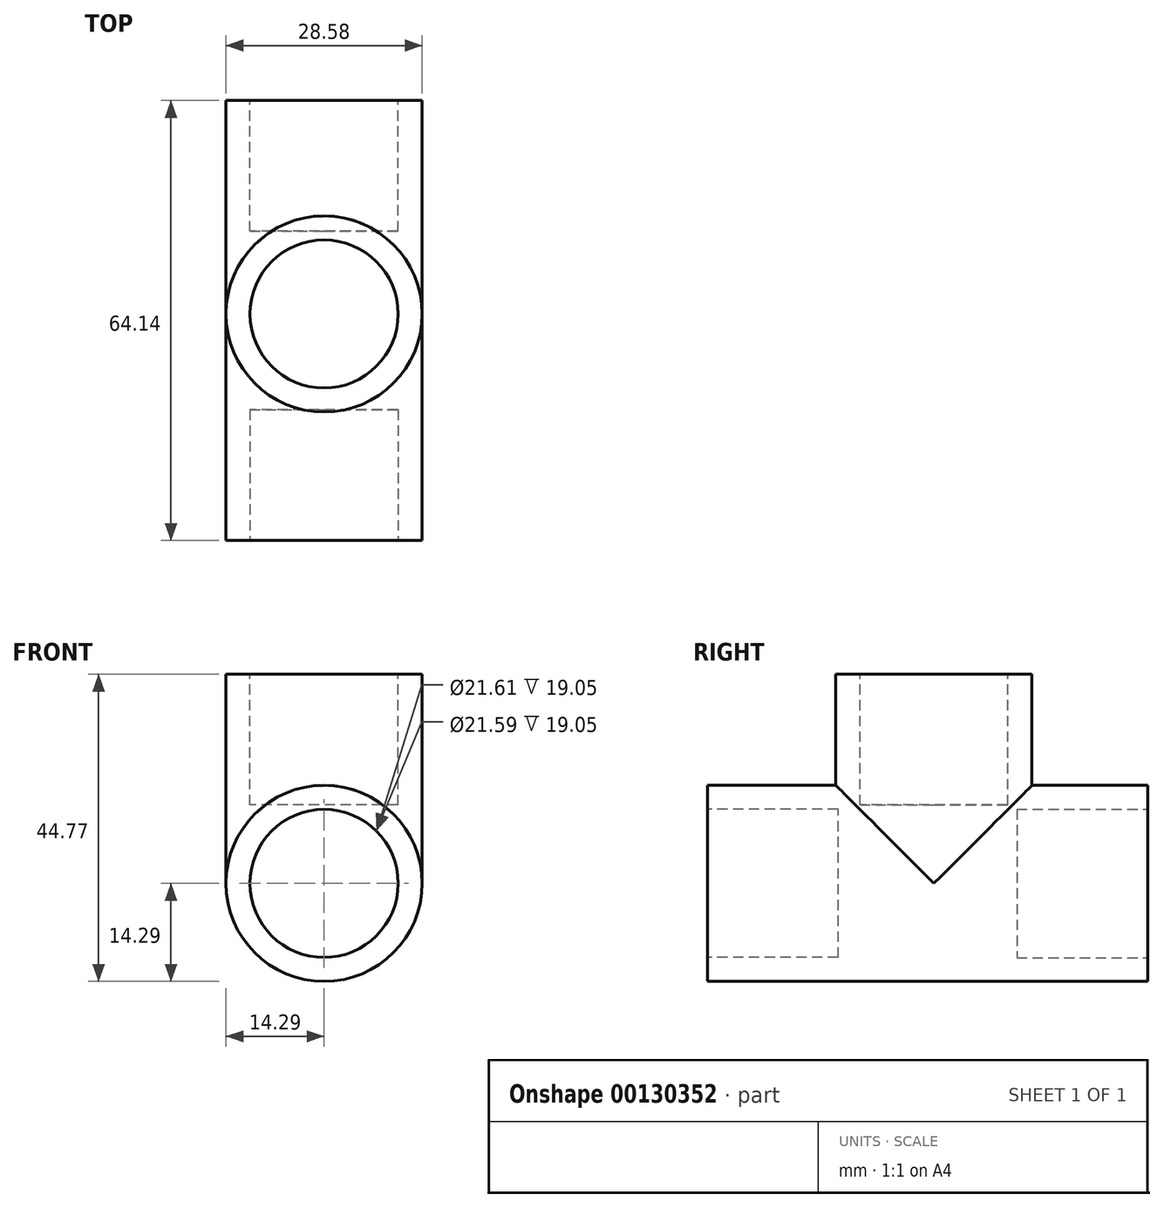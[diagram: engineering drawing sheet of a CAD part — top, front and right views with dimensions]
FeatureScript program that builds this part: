
annotation { "Feature Type Name" : "Feature", "Feature Type Description" : "" }
export const myFeature = defineFeature(function(context is Context, id is Id, definition is map)
    precondition{}
    {
        {
            var Q0;
            Q0=qCreatedBy(makeId("Front.planeOp"),FACE);
            var sketch = newSketch(context, id + "F0", { "sketchPlane" : qUnion([Q0])});
            skCircle(sketch, "E0", {"center": v(0, 0) * mm, "radius": 14.29 * mm});
            skSolve(sketch);
        }
        {
            var Q0;
            Q0=makeQuery(id+"F0.imprint","IMPRINT",FACE,{"disambiguationData":[TD([[makeQuery(id+"F0.imprint","IMPRINT",EDGE,{"derivedFrom":sQuery(id+"F0.wireOp",EDGE,"E0")}),1.0]])]});
            extrude(context, id + "F1", {"entities" : qUnion([Q0]), "depth" : 64.13 * mm});
        }
        {
            var Q0;
            Q0=makeQuery(id+"F1.opExtrude","CAP_FACE",FACE,{"disambiguationData":[OSD([sQuery(id+"F0.wireOp",EDGE,"E0")])],"isStart":false});
            var sketch = newSketch(context, id + "F2", { "sketchPlane" : qUnion([Q0])});
            skCircle(sketch, "E1", {"center": v(0, 0) * mm, "radius": 10.8 * mm});
            skSolve(sketch);
        }
        {
            var Q0;
            Q0=qCreatedBy(makeId("Top.planeOp"),FACE);
            var sketch = newSketch(context, id + "F3", { "sketchPlane" : qUnion([Q0])});
            skLineSegment(sketch, "E2", {"start": v(0, -62.15) * mm, "end": v(0, -31.12) * mm});
            skCircle(sketch, "E3", {"center": v(0, -31.12) * mm, "radius": 14.29 * mm});
            skSolve(sketch);
        }
        {
            var Q0;
            Q0 = qSketchRegion(id + "F3", true);
            extrude(context, id + "F4", {"entities" : qUnion([Q0]), "operationType" : NewBodyOperationType.ADD, "depth" : 30.48 * mm});
        }
        {
            var Q0;
            Q0=makeQuery(id+"F4.opExtrude","CAP_FACE",FACE,{"disambiguationData":[OSD([sQuery(id+"F3.wireOp",EDGE,"E3")])],"isStart":false});
            var sketch = newSketch(context, id + "F5", { "sketchPlane" : qUnion([Q0])});
            skCircle(sketch, "E4", {"center": v(0, -31.12) * mm, "radius": 10.8 * mm});
            skSolve(sketch);
        }
        {
            var Q0;
            Q0=makeQuery(id+"F1.opExtrude","CAP_FACE",FACE,{"disambiguationData":[OSD([sQuery(id+"F0.wireOp",EDGE,"E0")])],"isStart":true});
            var sketch = newSketch(context, id + "F6", { "sketchPlane" : qUnion([Q0])});
            skCircle(sketch, "E5", {"center": v(0, 0) * mm, "radius": 10.8 * mm});
            skSolve(sketch);
        }
        {
            var Q0;
            Q0=makeQuery(id+"F6.imprint","IMPRINT",FACE,{"disambiguationData":[TD([[makeQuery(id+"F6.imprint","IMPRINT",EDGE,{"derivedFrom":sQuery(id+"F6.wireOp",EDGE,"E5")}),1.0]])]});
            extrude(context, id + "F7", {"entities" : qUnion([Q0]), "operationType" : NewBodyOperationType.REMOVE, "oppositeDirection" : true, "depth" : 19.05 * mm});
        }
        {
            var Q0;
            Q0=makeQuery(id+"F5.imprint","IMPRINT",FACE,{"disambiguationData":[TD([[makeQuery(id+"F5.imprint","IMPRINT",EDGE,{"derivedFrom":sQuery(id+"F5.wireOp",EDGE,"E4")}),1.0]])]});
            extrude(context, id + "F8", {"entities" : qUnion([Q0]), "operationType" : NewBodyOperationType.REMOVE, "oppositeDirection" : true, "depth" : 19.05 * mm});
        }
        {
            var Q0;
            Q0=makeQuery(id+"F2.imprint","IMPRINT",FACE,{"disambiguationData":[TD([[makeQuery(id+"F2.imprint","IMPRINT",EDGE,{"derivedFrom":sQuery(id+"F2.wireOp",EDGE,"E1")}),1.0]])]});
            extrude(context, id + "F9", {"entities" : qUnion([Q0]), "operationType" : NewBodyOperationType.REMOVE, "oppositeDirection" : true, "depth" : 19.05 * mm});
        }
    });
